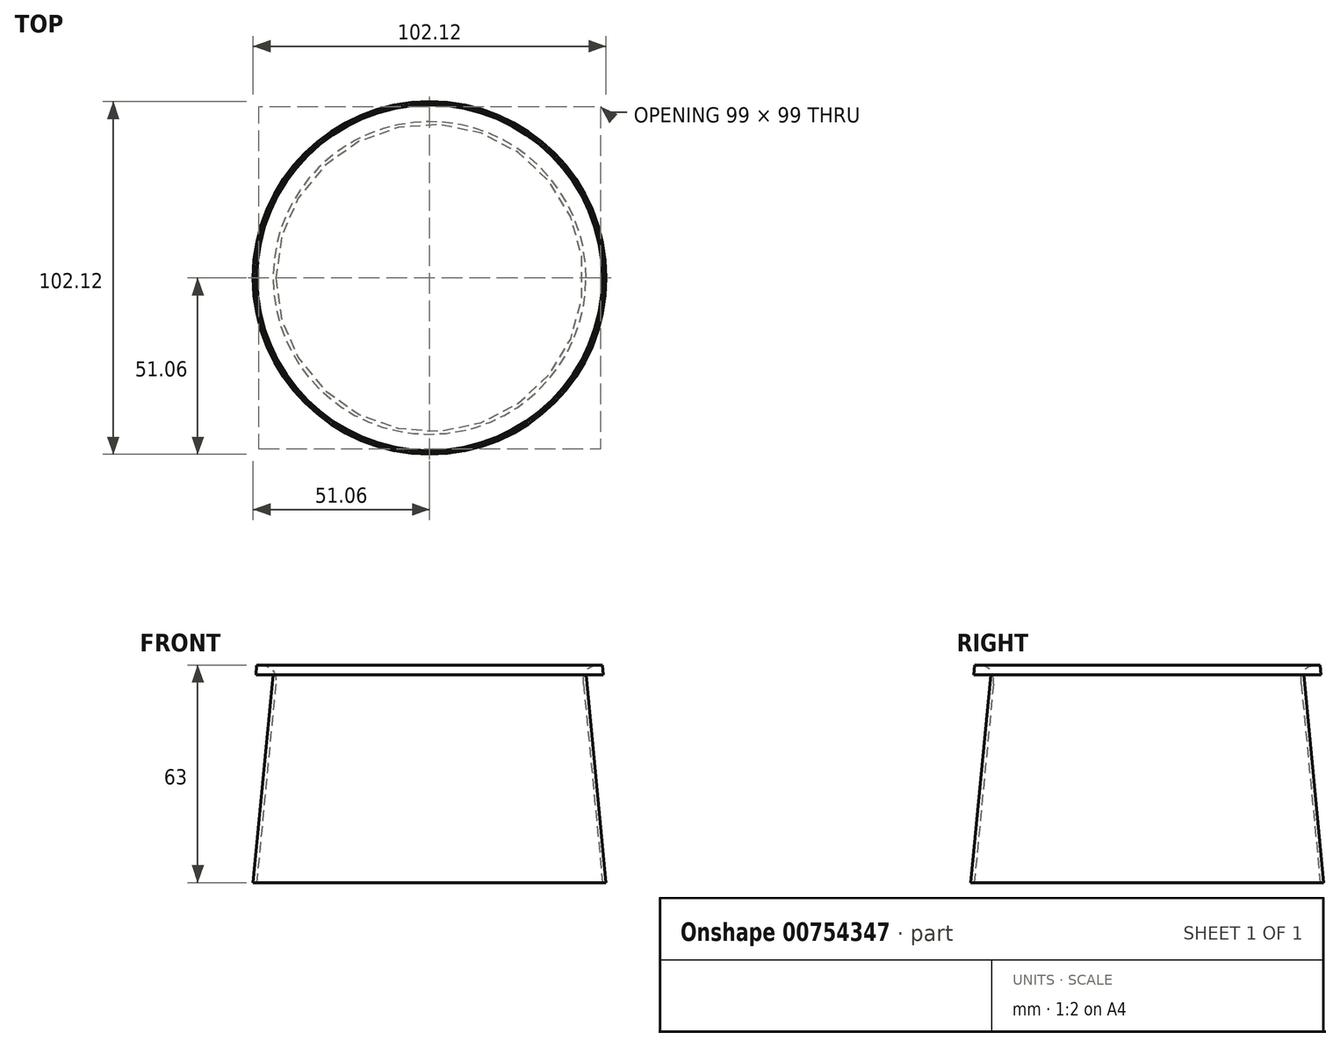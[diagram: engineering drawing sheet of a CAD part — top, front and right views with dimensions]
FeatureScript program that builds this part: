
annotation { "Feature Type Name" : "Feature", "Feature Type Description" : "" }
export const myFeature = defineFeature(function(context is Context, id is Id, definition is map)
    precondition{}
    {
        {
            var Q0;
            Q0=qCreatedBy(makeId("Front.planeOp"),FACE);
            var sketch = newSketch(context, id + "F0", { "sketchPlane" : qUnion([Q0])});
            skLineSegment(sketch, "E0", {"start": v(0, 0) * mm, "end": v(52.5, 0) * mm});
            skLineSegment(sketch, "E1", {"start": v(0, 0) * mm, "end": v(0, 78) * mm});
            skLineSegment(sketch, "E2", {"start": v(0, 78) * mm, "end": v(45, 78) * mm});
            skLineSegment(sketch, "E3", {"start": v(45, 78) * mm, "end": v(52.5, 0) * mm});
            skLineSegment(sketch, "E4", {"start": v(45, 78) * mm, "end": v(50, 78) * mm});
            skLineSegment(sketch, "E5", {"start": v(45.27, 75.2) * mm, "end": v(50.27, 75.2) * mm});
            skLineSegment(sketch, "E6", {"start": v(50.27, 75.2) * mm, "end": v(50, 78) * mm});
            skLineSegment(sketch, "E7", {"start": v(44, 78) * mm, "end": v(51.5, 0) * mm});
            skLineSegment(sketch, "E8", {"start": v(0, 15) * mm, "end": v(51.06, 15) * mm});
            skSolve(sketch);
        }
        {
            var Q0;
            {var subQ0=sQuery(id+"F0.wireOp",EDGE,"E4");Q0=makeQuery(id+"F0.imprint","IMPRINT",FACE,{"disambiguationData":[TD([[makeQuery(id+"F0.imprint","IMPRINT",EDGE,{"derivedFrom":subQ0}),-1.0]])]});}
            var Q1;
            {var subQ5=sQuery(id+"F0.wireOp",EDGE,"E3");var subQ6=makeQuery(id+"F0.imprint","INTERSECT",VERTEX,{"derivedFrom":[subQ5,sQuery(id+"F0.wireOp",EDGE,"E5")]});Q1=makeQuery(id+"F0.imprint","IMPRINT",FACE,{"disambiguationData":[TD([[makeQuery(id+"F0.imprint","IMPRINT",EDGE,{"disambiguationData":[TD([[subQ6,-1.0]])],"derivedFrom":subQ5}),-1.0]])]});}
            var Q2;
            Q2=sQuery(id+"F0.wireOp",EDGE,"E1");
            revolve(context, id + "F1", {"surfaceOperationType" : NewSurfaceOperationType.NEW, "entities" : qUnion([Q0, Q1]), "axis" : qUnion([Q2]), "revolveType" : RevolveType.FULL});
        }
        {
            var Q0;
            Q0=makeQuery(id+"F1.opRevolve","SWEPT_EDGE",EDGE,{"disambiguationData":[OSD([sQuery(id+"F0.wireOp",EDGE,"E2"),sQuery(id+"F0.wireOp",EDGE,"E7")])]});
            fillet(context, id + "F2", {"entities" : qUnion([Q0]), "radius" : 5 * mm, "tangentPropagation" : true, "rho" : 0.5, "crossSection" : FilletCrossSection.CONIC, "allowEdgeOverflow" : false});
        }
    });
